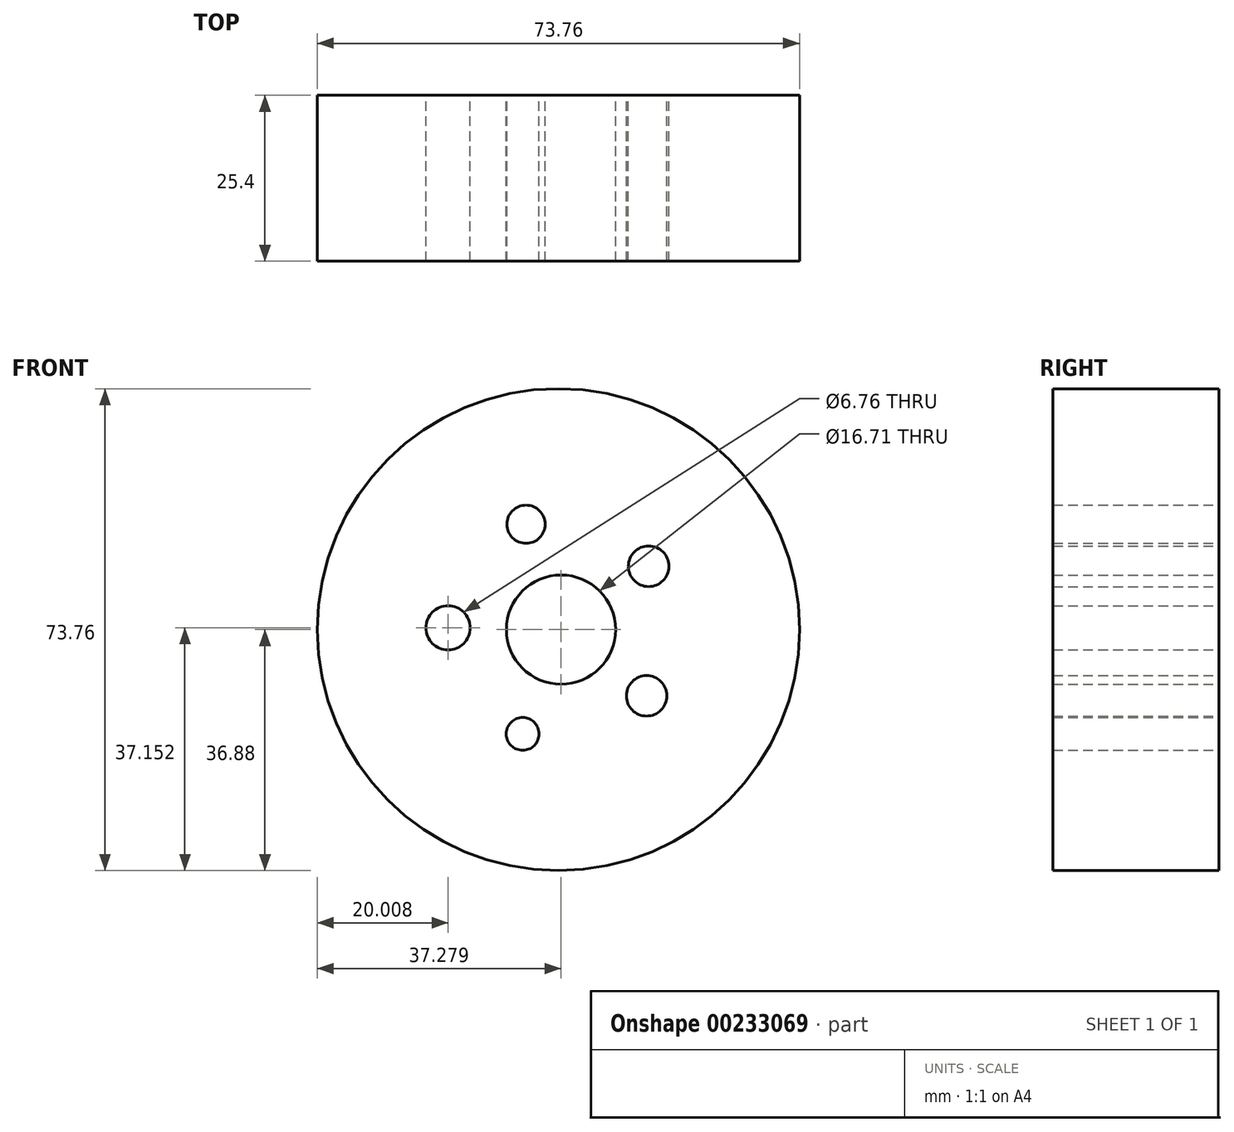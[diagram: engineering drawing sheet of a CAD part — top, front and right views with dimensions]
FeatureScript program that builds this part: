
annotation { "Feature Type Name" : "Feature", "Feature Type Description" : "" }
export const myFeature = defineFeature(function(context is Context, id is Id, definition is map)
    precondition{}
    {
        {
            var Q0;
            Q0=qCreatedBy(makeId("Front.planeOp"),FACE);
            var sketch = newSketch(context, id + "F0", { "sketchPlane" : qUnion([Q0])});
            skArc(sketch, "E0", {"start": v(-4.9, 16.11) * mm, "mid": v(-4.95, 16.1) * mm, "end": v(-4.99, 16.09) * mm});
            skCircle(sketch, "E1", {"center": v(0, 0) * mm, "radius": 36.88 * mm});
            skLineSegment(sketch, "E2.0", {"start": v(-16.87, 0.27) * mm, "end": v(-16.84, 0.31) * mm});
            skLineSegment(sketch, "E2.1", {"start": v(-4.95, 16.13) * mm, "end": v(-4.9, 16.11) * mm});
            skLineSegment(sketch, "E2.2", {"start": v(13.8, 9.7) * mm, "end": v(13.8, 9.64) * mm});
            skLineSegment(sketch, "E2.3", {"start": v(13.49, -10.14) * mm, "end": v(13.44, -10.15) * mm});
            skLineSegment(sketch, "E2.4", {"start": v(-5.47, -15.96) * mm, "end": v(-5.5, -15.92) * mm});
            skCircle(sketch, "E3", {"center": v(-4.95, 16.13) * mm, "radius": 2.92 * mm});
            skCircle(sketch, "E4", {"center": v(13.8, 9.7) * mm, "radius": 3.11 * mm});
            skCircle(sketch, "E5", {"center": v(13.49, -10.14) * mm, "radius": 3.1 * mm});
            skCircle(sketch, "E6", {"center": v(-5.47, -15.96) * mm, "radius": 2.51 * mm});
            skCircle(sketch, "E7", {"center": v(-16.87, 0.27) * mm, "radius": 3.38 * mm});
            skLineSegment(sketch, "E8.trimOffspring", {"start": v(13.76, 9.71) * mm, "end": v(13.8, 9.7) * mm});
            skLineSegment(sketch, "E9.trimOffspring", {"start": v(-4.99, 16.09) * mm, "end": v(-4.95, 16.13) * mm});
            skArc(sketch, "E10.trimOffspring", {"start": v(13.8, 9.64) * mm, "mid": v(13.78, 9.68) * mm, "end": v(13.76, 9.71) * mm});
            skLineSegment(sketch, "E11.trimOffspring", {"start": v(13.5, -10.08) * mm, "end": v(13.49, -10.14) * mm});
            skArc(sketch, "E12.trimOffspring", {"start": v(13.44, -10.15) * mm, "mid": v(13.46, -10.12) * mm, "end": v(13.5, -10.08) * mm});
            skLineSegment(sketch, "E13.trimOffspring", {"start": v(-5.42, -15.95) * mm, "end": v(-5.47, -15.96) * mm});
            skArc(sketch, "E14.trimOffspring", {"start": v(-5.5, -15.92) * mm, "mid": v(-5.46, -15.93) * mm, "end": v(-5.42, -15.95) * mm});
            skLineSegment(sketch, "E15.trimOffspring", {"start": v(-16.84, 0.23) * mm, "end": v(-16.87, 0.27) * mm});
            skArc(sketch, "E16.trimOffspring", {"start": v(-16.84, 0.31) * mm, "mid": v(-16.84, 0.27) * mm, "end": v(-16.84, 0.23) * mm});
            skCircle(sketch, "E17", {"center": v(0.4, 0) * mm, "radius": 8.36 * mm});
            skSolve(sketch);
        }
        {
            var Q0;
            Q0=makeQuery(id+"F0.imprint","IMPRINT",FACE,{"disambiguationData":[TD([[makeQuery(id+"F0.imprint","IMPRINT",EDGE,{"derivedFrom":sQuery(id+"F0.wireOp",EDGE,"E1")}),1.0]])]});
            extrude(context, id + "F1", {"entities" : qUnion([Q0]), "depth" : 25.4 * mm});
        }
    });
